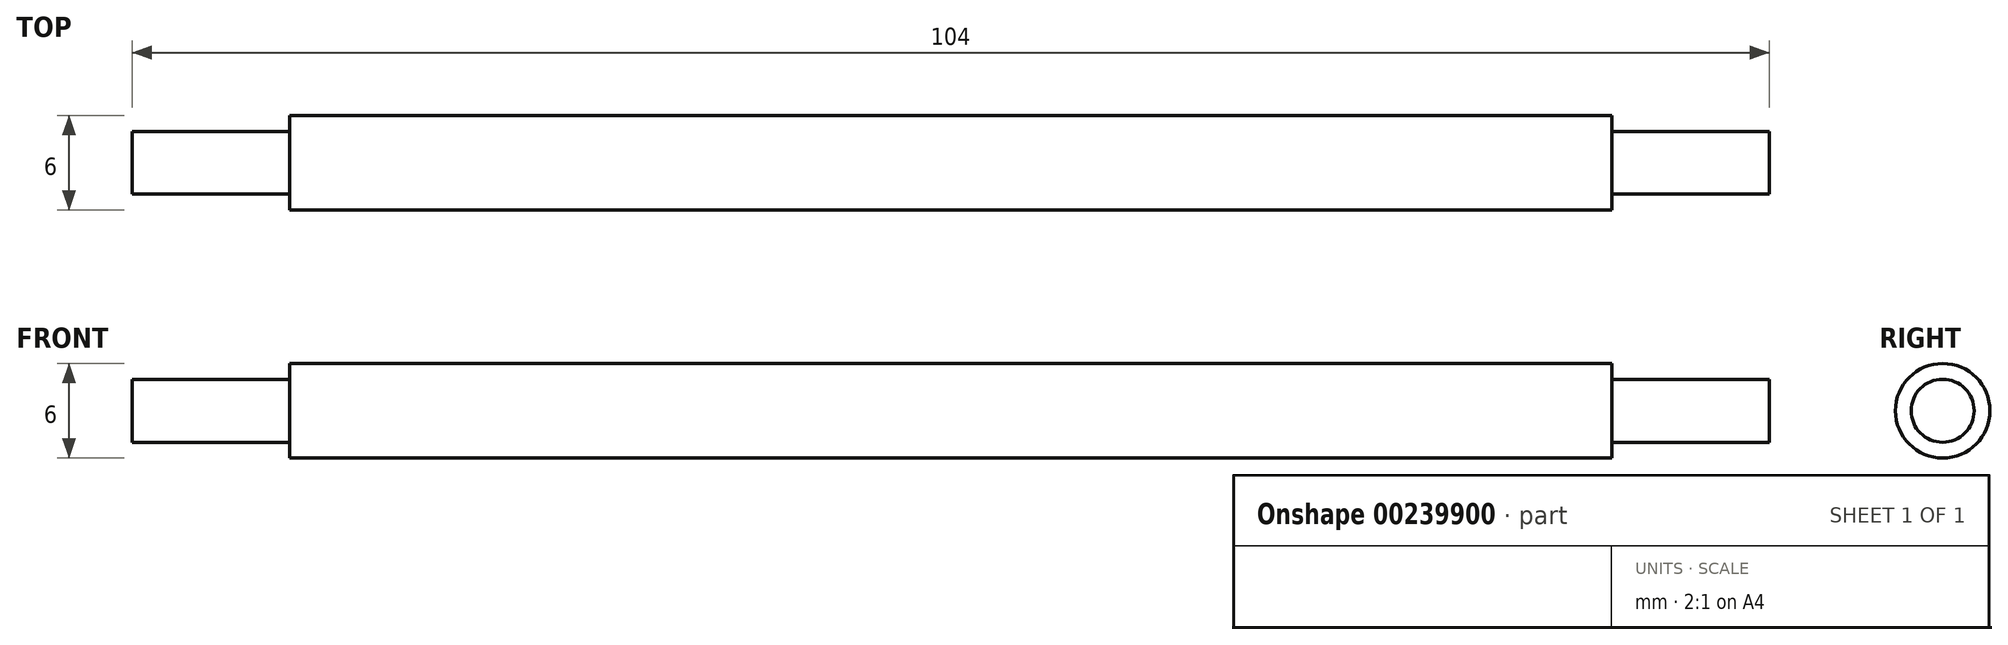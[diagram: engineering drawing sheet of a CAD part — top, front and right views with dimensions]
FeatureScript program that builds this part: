
annotation { "Feature Type Name" : "Feature", "Feature Type Description" : "" }
export const myFeature = defineFeature(function(context is Context, id is Id, definition is map)
    precondition{}
    {
        {
            var Q0;
            Q0=qCreatedBy(makeId("Front.planeOp"),FACE);
            var sketch = newSketch(context, id + "F0", { "sketchPlane" : qUnion([Q0])});
            skLineSegment(sketch, "E0", {"start": v(-52, 0) * mm, "end": v(-52, 2) * mm});
            skLineSegment(sketch, "E1", {"start": v(-52, 2) * mm, "end": v(-42, 2) * mm});
            skLineSegment(sketch, "E2", {"start": v(-42, 2) * mm, "end": v(-42, 3) * mm});
            skLineSegment(sketch, "E3", {"start": v(-42, 3) * mm, "end": v(42, 3) * mm});
            skLineSegment(sketch, "E4", {"start": v(42, 3) * mm, "end": v(42, 2) * mm});
            skLineSegment(sketch, "E5", {"start": v(42, 2) * mm, "end": v(52, 2) * mm});
            skLineSegment(sketch, "E6", {"start": v(52, 2) * mm, "end": v(52, 0) * mm});
            skLineSegment(sketch, "E7", {"start": v(52, 0) * mm, "end": v(-52, 0) * mm});
            skPoint(sketch, "E8", {"position": v(0, 0) * mm});
            skSolve(sketch);
        }
        {
            var Q0;
            Q0 = qSketchRegion(id + "F0", true);
            var Q1;
            Q1=sQuery(id+"F0.wireOp",EDGE,"E7");
            revolve(context, id + "F1", {"entities" : qUnion([Q0]), "axis" : qUnion([Q1]), "revolveType" : RevolveType.FULL});
        }
    });
